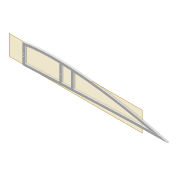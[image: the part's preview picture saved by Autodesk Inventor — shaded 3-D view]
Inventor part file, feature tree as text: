
AUTODESK INVENTOR PART (.ipt)
format: ipt  version: 2022 (Build 260153000, 153)  size: 362,496 bytes
history: native  units: mm
features: extrude x7, sketch x7, projected_geometry x5, shell x1, fillet x1, plane x1
ambient origin geometry x8: Origin, YZ Plane, XZ Plane, XY Plane, X Axis, Y Axis, Z Axis, Center Point
bodies: Solid1 (feature_tree)
feature tree (22):
  extrude  "Extrusion1"  Depth=5.0mm
  shell  "Shell1"  Thickness=2.0mm
  extrude  "Extrusion8"  Depth=5.9mm
  extrude  "Extrusion3"  Depth=10.0mm TaperAngle=0.0deg
  extrude  "Extrusion4"  Depth=2.0mm
  fillet  "Fillet1"  Radius=5.0mm
  extrude  "Extrusion5"  Depth=2.5mm
  plane  "Work Plane2"
  extrude  "Extrusion9"  Depth=1.6mm
  extrude  "Extrusion10"  Depth=0.5mm
  sketch  "Sketch3"  dims[d0=4.0mm d1=0.0mm d2=5.0mm d7=2.0mm]
  sketch  "Sketch8"  dims[d8=2.0mm d9=5.9mm]
  sketch  "Sketch9"  dims[d13=10.0mm d14=0.0mm d16=10.0mm d17=0.0mm]
  sketch  "Sketch10"  dims[d22=4.0mm d23=0.0mm d31=2.0mm d32=5.0mm]
  projected_geometry  "Projected Loop4"
  projected_geometry  "Projected Loop10"
  sketch  "Sketch24"  dims[d34=1.6mm d35=2.5mm]
  projected_geometry  "Projected Loop11"
  projected_geometry  "Projected Loop12"
  sketch  "Sketch26"  dims[d37=5.0mm d38=1.6mm]
  projected_geometry  "Projected Loop13"
  sketch  "Sketch27"  dims[d40=2.5mm d62=67.0mm d63=6.0mm d64=4.0mm d65=0.0mm d66=3.0mm d67=12.0mm d68=75.0mm d69=20.0mm d70=0.5mm d71=10.0mm d72=0.0mm d73=10.0mm d74=0.0mm]
